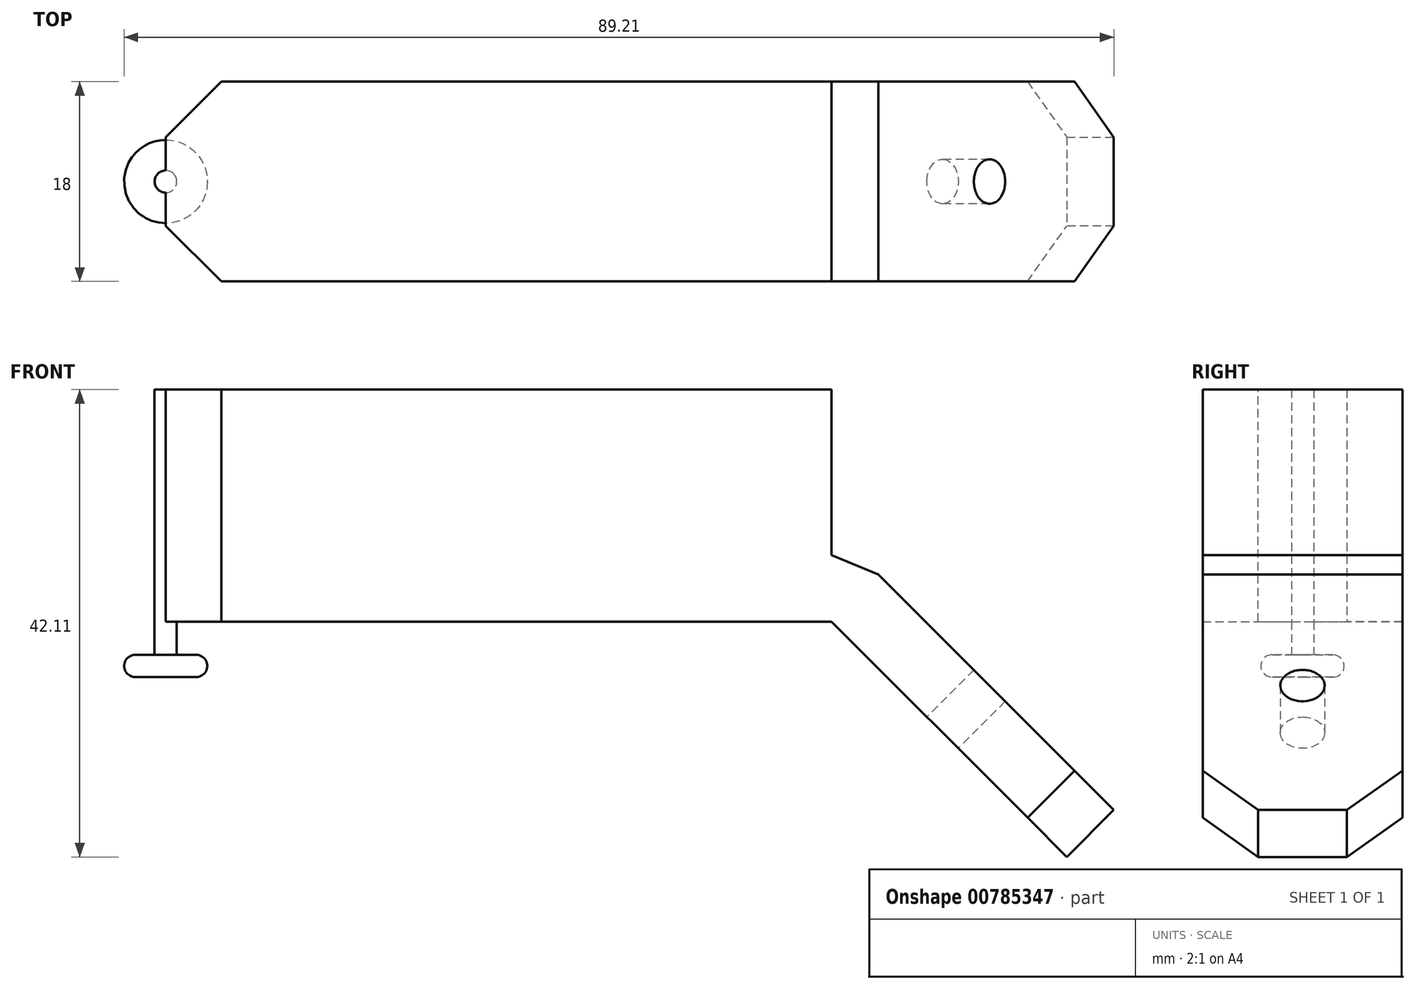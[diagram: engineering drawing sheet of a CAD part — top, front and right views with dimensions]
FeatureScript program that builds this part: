
annotation { "Feature Type Name" : "Feature", "Feature Type Description" : "" }
export const myFeature = defineFeature(function(context is Context, id is Id, definition is map)
    precondition{}
    {
        {
            var Q0;
            Q0=qCreatedBy(makeId("Top.planeOp"),FACE);
            var sketch = newSketch(context, id + "F0", { "sketchPlane" : qUnion([Q0])});
            skCircle(sketch, "E0", {"center": v(0, 0) * mm, "radius": 3.75 * mm});
            skSolve(sketch);
        }
        {
            var Q0;
            Q0=makeQuery(id+"F0.imprint","IMPRINT",FACE,{"disambiguationData":[TD([[makeQuery(id+"F0.imprint","IMPRINT",EDGE,{"derivedFrom":sQuery(id+"F0.wireOp",EDGE,"E0")}),1.0]])]});
            extrude(context, id + "F1", {"entities" : qUnion([Q0]), "depth" : 2 * mm, "offsetDistance" : 25 * mm});
        }
        {
            var Q0;
            Q0=makeQuery(id+"F1.opExtrude","CAP_FACE",FACE,{"disambiguationData":[OSD([sQuery(id+"F0.wireOp",EDGE,"E0")])],"isStart":false});
            var sketch = newSketch(context, id + "F2", { "sketchPlane" : qUnion([Q0])});
            skCircle(sketch, "E1", {"center": v(0, 0) * mm, "radius": 1 * mm});
            skSolve(sketch);
        }
        {
            var Q0;
            Q0=makeQuery(id+"F2.imprint","IMPRINT",FACE,{"disambiguationData":[TD([[makeQuery(id+"F2.imprint","IMPRINT",EDGE,{"derivedFrom":sQuery(id+"F2.wireOp",EDGE,"E1")}),1.0]])]});
            extrude(context, id + "F3", {"entities" : qUnion([Q0]), "operationType" : NewBodyOperationType.ADD, "depth" : 3 * mm, "offsetDistance" : 25 * mm});
        }
        {
            var Q0;
            Q0=makeQuery(id+"F3.opExtrude","CAP_FACE",FACE,{"disambiguationData":[OSD([sQuery(id+"F2.wireOp",EDGE,"E1")])],"isStart":false});
            var sketch = newSketch(context, id + "F4", { "sketchPlane" : qUnion([Q0])});
            skLineSegment(sketch, "E2.bottom", {"start": v(-22.5, 9) * mm, "end": v(22.5, 9) * mm});
            skLineSegment(sketch, "E2.top", {"start": v(-22.5, -9) * mm, "end": v(22.5, -9) * mm});
            skLineSegment(sketch, "E2.left", {"start": v(-22.5, 9) * mm, "end": v(-22.5, -9) * mm});
            skLineSegment(sketch, "E2.right", {"start": v(22.5, 9) * mm, "end": v(22.5, -9) * mm});
            skPoint(sketch, "E2.middle", {"position": v(0, 0) * mm});
            skLineSegment(sketch, "E3.bottom", {"start": v(0, -9) * mm, "end": v(60, -9) * mm});
            skLineSegment(sketch, "E3.top", {"start": v(0, 9) * mm, "end": v(60, 9) * mm});
            skLineSegment(sketch, "E3.left", {"start": v(0, -9) * mm, "end": v(0, 9) * mm});
            skLineSegment(sketch, "E3.right", {"start": v(60, -9) * mm, "end": v(60, 9) * mm});
            skLineSegment(sketch, "E4", {"start": v(0, -9) * mm, "end": v(-6, -9) * mm});
            skLineSegment(sketch, "E5", {"start": v(-6, -9) * mm, "end": v(-6, 9) * mm});
            skSolve(sketch);
        }
        {
            var Q0;
            {var subQ3=sQuery(id+"F4.wireOp",EDGE,"E2.right");Q0=makeQuery(id+"F4.imprint","IMPRINT",FACE,{"disambiguationData":[TD([[makeQuery(id+"F4.imprint","IMPRINT",EDGE,{"derivedFrom":subQ3}),-1.0]])]});}
            var Q1;
            {var subQ0=sQuery(id+"F4.wireOp",EDGE,"E3.left");var subQ1=makeQuery(id+"F3.opExtrude","CAP_EDGE",EDGE,{"disambiguationData":[OSD([sQuery(id+"F2.wireOp",EDGE,"E1")])],"isStart":false});var subQ2=makeQuery(id+"F4.imprint","INTERSECT",VERTEX,{"disambiguationData":[OD(0.0)],"derivedFrom":[subQ1,subQ0]});Q1=makeQuery(id+"F4.imprint","IMPRINT",FACE,{"disambiguationData":[TD([[makeQuery(id+"F4.imprint","IMPRINT",EDGE,{"disambiguationData":[TD([[subQ2,-1.0]])],"derivedFrom":subQ0}),-1.0]])]});}
            var Q2;
            {var subQ0=sQuery(id+"F4.wireOp",EDGE,"E3.left");var subQ1=makeQuery(id+"F3.opExtrude","CAP_EDGE",EDGE,{"disambiguationData":[OSD([sQuery(id+"F2.wireOp",EDGE,"E1")])],"isStart":false});var subQ2=makeQuery(id+"F4.imprint","INTERSECT",VERTEX,{"disambiguationData":[OD(0.0)],"derivedFrom":[subQ1,subQ0]});Q2=makeQuery(id+"F4.imprint","IMPRINT",FACE,{"disambiguationData":[TD([[makeQuery(id+"F4.imprint","IMPRINT",EDGE,{"disambiguationData":[TD([[subQ2,-1.0]])],"derivedFrom":subQ0}),1.0]])]});}
            var Q3;
            {var subQ0=sQuery(id+"F4.wireOp",EDGE,"E4");Q3=makeQuery(id+"F4.imprint","IMPRINT",FACE,{"disambiguationData":[TD([[makeQuery(id+"F4.imprint","IMPRINT",EDGE,{"derivedFrom":subQ0}),-1.0]])]});}
            var Q4;
            {var subQ0=sQuery(id+"F4.wireOp",EDGE,"E2.right");Q4=makeQuery(id+"F4.imprint","IMPRINT",FACE,{"disambiguationData":[TD([[makeQuery(id+"F4.imprint","IMPRINT",EDGE,{"derivedFrom":subQ0}),1.0]])]});}
            extrude(context, id + "F5", {"entities" : qUnion([Q0, Q1, Q2, Q3, Q4]), "operationType" : NewBodyOperationType.ADD, "depth" : 6 * mm, "offsetDistance" : 25 * mm});
        }
        {
            var Q0;
            Q0=makeQuery(id+"F5.opExtrude","SWEPT_FACE",FACE,{"disambiguationData":[OSD([sQuery(id+"F4.wireOp",EDGE,"E3.bottom"),sQuery(id+"F4.wireOp",EDGE,"E4")])]});
            var sketch = newSketch(context, id + "F6", { "sketchPlane" : qUnion([Q0])});
            skLineSegment(sketch, "E6", {"start": v(60, 5) * mm, "end": v(64.24, 9.24) * mm});
            skLineSegment(sketch, "E7", {"start": v(64.24, 9.24) * mm, "end": v(60, 11) * mm});
            skLineSegment(sketch, "E8", {"start": v(64.24, 9.24) * mm, "end": v(85.46, -11.97) * mm});
            skLineSegment(sketch, "E9", {"start": v(85.46, -11.97) * mm, "end": v(81.21, -16.21) * mm});
            skLineSegment(sketch, "E10", {"start": v(81.21, -16.21) * mm, "end": v(60, 5) * mm});
            skSolve(sketch);
        }
        {
            var Q0;
            Q0=makeQuery(id+"F6.imprint","IMPRINT",FACE,{"disambiguationData":[TD([[makeQuery(id+"F6.imprint","IMPRINT",EDGE,{"derivedFrom":sQuery(id+"F6.wireOp",EDGE,"E6")}),-1.0]])]});
            var Q1;
            Q1=makeQuery(id+"F6.imprint","IMPRINT",FACE,{"disambiguationData":[TD([[makeQuery(id+"F6.imprint","IMPRINT",EDGE,{"derivedFrom":sQuery(id+"F6.wireOp",EDGE,"E6")}),1.0]])]});
            extrude(context, id + "F7", {"entities" : qUnion([Q0, Q1]), "operationType" : NewBodyOperationType.ADD, "oppositeDirection" : true, "depth" : 18 * mm, "offsetDistance" : 25 * mm});
        }
        {
            var Q0;
            Q0=makeQuery(id+"F7.opExtrude","SWEPT_FACE",FACE,{"disambiguationData":[OSD([sQuery(id+"F6.wireOp",EDGE,"E10")])]});
            var sketch = newSketch(context, id + "F8", { "sketchPlane" : qUnion([Q0])});
            skCircle(sketch, "E11", {"center": v(0, -53.05) * mm, "radius": 2 * mm});
            skPoint(sketch, "E11.centerSnap0", {"position": v(0, -68.9) * mm});
            skSolve(sketch);
        }
        {
            var Q0;
            Q0=makeQuery(id+"F8.imprint","IMPRINT",FACE,{"disambiguationData":[TD([[makeQuery(id+"F8.imprint","IMPRINT",EDGE,{"derivedFrom":sQuery(id+"F8.wireOp",EDGE,"E11")}),1.0]])]});
            extrude(context, id + "F9", {"entities" : qUnion([Q0]), "operationType" : NewBodyOperationType.REMOVE, "oppositeDirection" : true, "depth" : 37.8 * mm, "offsetDistance" : 25 * mm});
        }
        {
            var Q0;
            Q0=makeQuery(id+"F1.opExtrude","CAP_EDGE",EDGE,{"disambiguationData":[OSD([sQuery(id+"F0.wireOp",EDGE,"E0")])],"isStart":true});
            var Q1;
            Q1=makeQuery(id+"F1.opExtrude","CAP_EDGE",EDGE,{"disambiguationData":[OSD([sQuery(id+"F0.wireOp",EDGE,"E0")])],"isStart":false});
            fillet(context, id + "F10", {"entities" : qUnion([Q0, Q1]), "radius" : 1 * mm, "tangentPropagation" : true, "allowEdgeOverflow" : false});
        }
        {
            var Q0;
            Q0=makeQuery(id+"F5.opExtrude","SWEPT_EDGE",EDGE,{"disambiguationData":[OSD([sQuery(id+"F4.wireOp",EDGE,"E2.top"),sQuery(id+"F4.wireOp",EDGE,"E4"),sQuery(id+"F4.wireOp",EDGE,"E5")])]});
            var Q1;
            Q1=makeQuery(id+"F5.opExtrude","SWEPT_EDGE",EDGE,{"disambiguationData":[OSD([sQuery(id+"F4.wireOp",EDGE,"E2.bottom"),sQuery(id+"F4.wireOp",EDGE,"E5")])]});
            var Q2;
            Q2=makeQuery(id+"F7.opExtrude","CAP_EDGE",EDGE,{"disambiguationData":[OSD([sQuery(id+"F6.wireOp",EDGE,"E9")])],"isStart":false});
            var Q3;
            Q3=makeQuery(id+"F7.opExtrude","CAP_EDGE",EDGE,{"disambiguationData":[OSD([sQuery(id+"F6.wireOp",EDGE,"E9")])],"isStart":true});
            chamfer(context, id + "F11", {"entities" : qUnion([Q0, Q1, Q2, Q3]), "width" : 5 * mm, "tangentPropagation" : true});
        }
        {
            var Q0;
            Q0=makeQuery(id+"F5.opExtrude","CAP_FACE",FACE,{"disambiguationData":[OSD([sQuery(id+"F4.wireOp",EDGE,"E2.bottom"),sQuery(id+"F4.wireOp",EDGE,"E3.bottom"),sQuery(id+"F4.wireOp",EDGE,"E3.top"),sQuery(id+"F4.wireOp",EDGE,"E3.right"),sQuery(id+"F4.wireOp",EDGE,"E4"),sQuery(id+"F4.wireOp",EDGE,"E5")])],"isStart":false});
            extrude(context, id + "F12", {"entities" : qUnion([Q0]), "operationType" : NewBodyOperationType.ADD, "depth" : 14.9 * mm, "offsetDistance" : 25 * mm});
        }
    });
